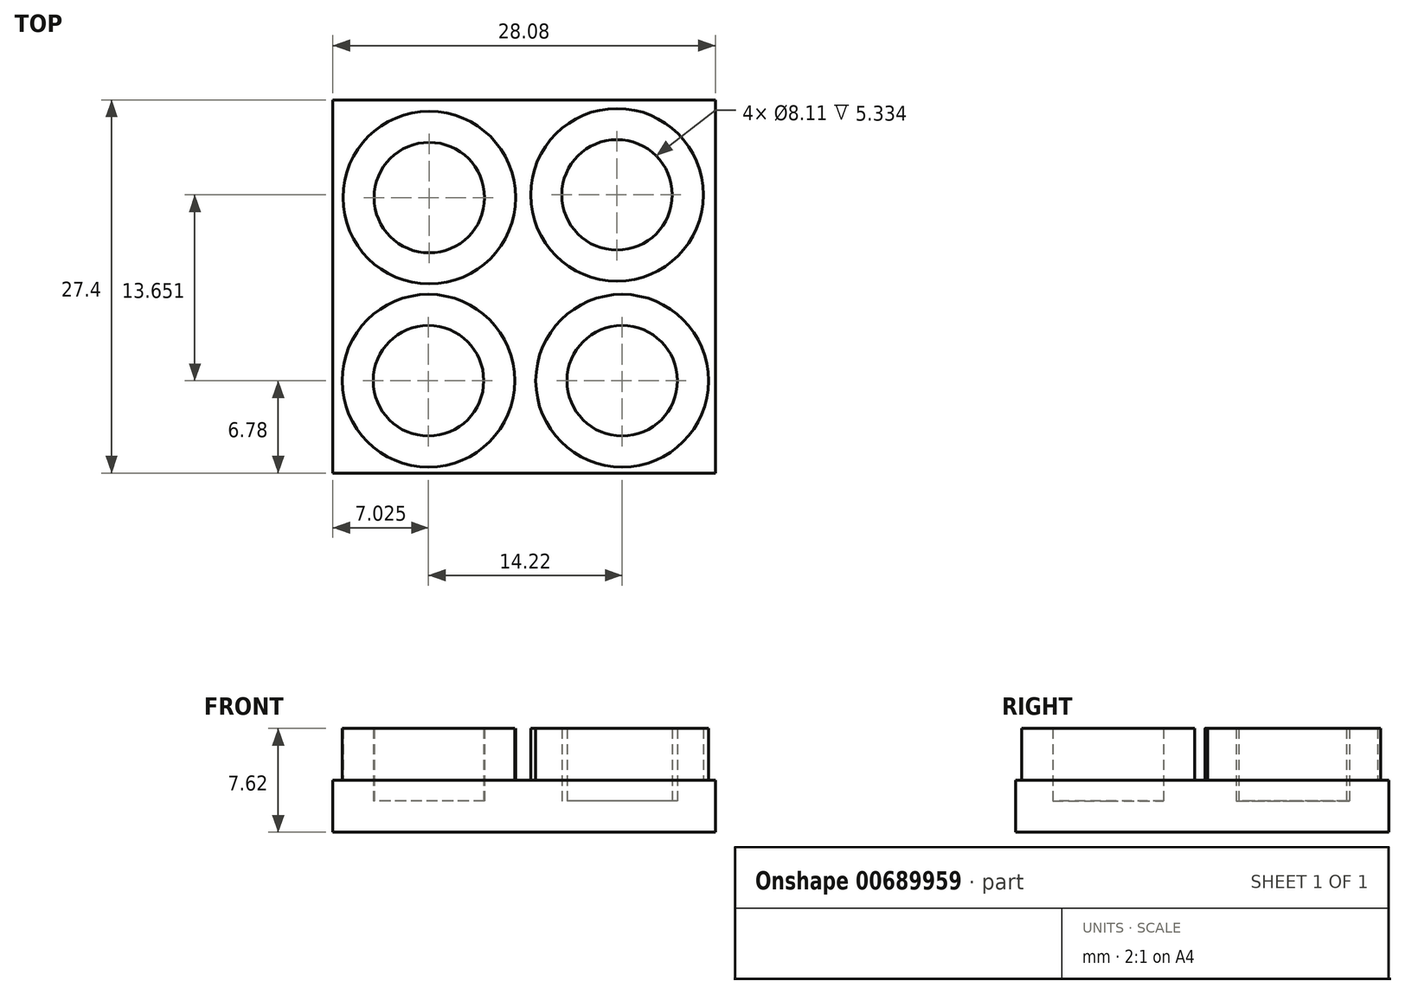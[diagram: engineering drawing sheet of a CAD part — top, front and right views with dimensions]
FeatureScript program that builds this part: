
annotation { "Feature Type Name" : "Feature", "Feature Type Description" : "" }
export const myFeature = defineFeature(function(context is Context, id is Id, definition is map)
    precondition{}
    {
        {
            var Q0;
            Q0=qCreatedBy(makeId("Top.planeOp"),FACE);
            var sketch = newSketch(context, id + "F0", { "sketchPlane" : qUnion([Q0])});
            skLineSegment(sketch, "E0.bottom", {"start": v(14.04, -13.7) * mm, "end": v(-14.04, -13.7) * mm});
            skLineSegment(sketch, "E0.top", {"start": v(14.04, 13.7) * mm, "end": v(-14.04, 13.7) * mm});
            skLineSegment(sketch, "E0.left", {"start": v(14.04, -13.7) * mm, "end": v(14.04, 13.7) * mm});
            skLineSegment(sketch, "E0.right", {"start": v(-14.04, -13.7) * mm, "end": v(-14.04, 13.7) * mm});
            skPoint(sketch, "E0.middle", {"position": v(0, 0) * mm});
            skSolve(sketch);
        }
        {
            var Q0;
            Q0 = qSketchRegion(id + "F0", true);
            extrude(context, id + "F1", {"entities" : qUnion([Q0]), "depth" : 3.8 * mm, "offsetDistance" : 25.4 * mm});
        }
        {
            var Q0;
            Q0=qCreatedBy(makeId("Top.planeOp"),FACE);
            var sketch = newSketch(context, id + "F2", { "sketchPlane" : qUnion([Q0])});
            skCircle(sketch, "E1", {"center": v(-6.95, 6.53) * mm, "radius": 6.34 * mm});
            skCircle(sketch, "E2", {"center": v(6.83, 6.73) * mm, "radius": 6.34 * mm});
            skCircle(sketch, "E3", {"center": v(7.2, -6.92) * mm, "radius": 6.34 * mm});
            skCircle(sketch, "E4", {"center": v(-7.02, -6.92) * mm, "radius": 6.34 * mm});
            skSolve(sketch);
        }
        {
            var Q0;
            Q0 = qSketchRegion(id + "F2", true);
            extrude(context, id + "F3", {"entities" : qUnion([Q0]), "operationType" : NewBodyOperationType.ADD, "depth" : 7.62 * mm, "offsetDistance" : 25.4 * mm});
        }
        {
            var Q0;
            Q0=makeQuery(id+"F3.opExtrude","CAP_FACE",FACE,{"disambiguationData":[OSD([sQuery(id+"F2.wireOp",EDGE,"E1")])],"isStart":false});
            var Q1;
            Q1=makeQuery(id+"F3.opExtrude","CAP_FACE",FACE,{"disambiguationData":[OSD([sQuery(id+"F2.wireOp",EDGE,"E4")])],"isStart":false});
            var Q2;
            Q2=makeQuery(id+"F3.opExtrude","CAP_FACE",FACE,{"disambiguationData":[OSD([sQuery(id+"F2.wireOp",EDGE,"E3")])],"isStart":false});
            var Q3;
            Q3=makeQuery(id+"F3.opExtrude","CAP_FACE",FACE,{"disambiguationData":[OSD([sQuery(id+"F2.wireOp",EDGE,"E2")])],"isStart":false});
            shell(context, id + "F4", {"entities" : qUnion([Q0, Q1, Q2, Q3]), "thickness" : 2.3 * mm});
        }
    });
